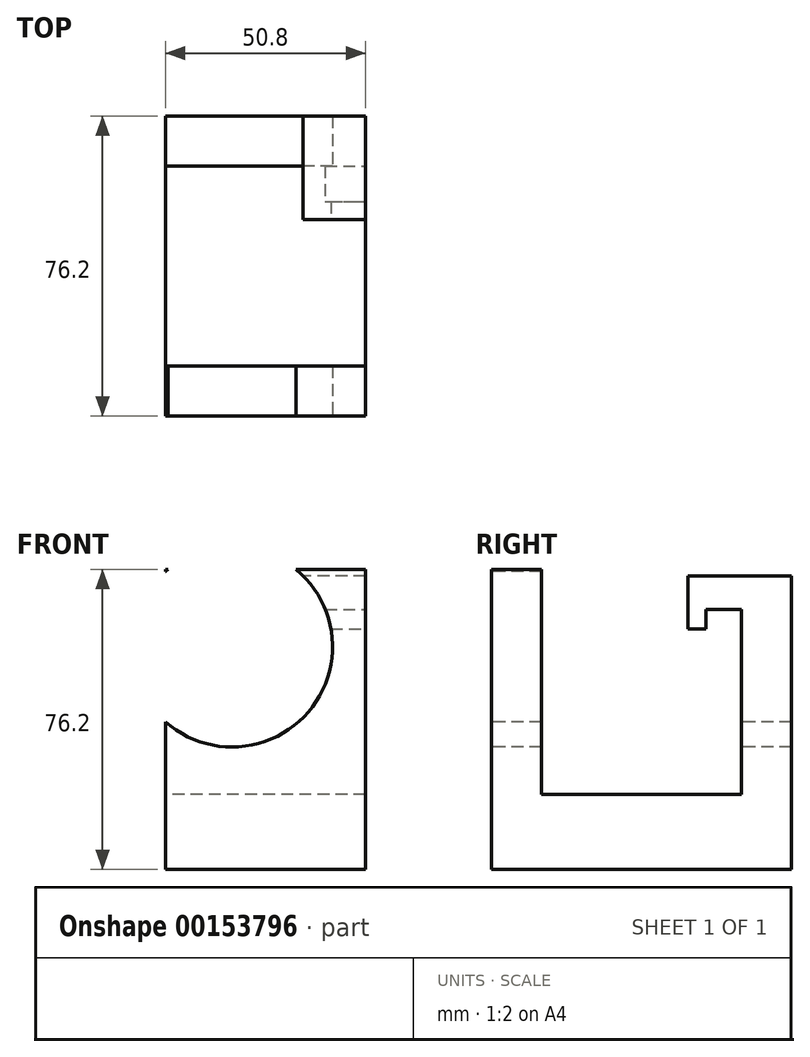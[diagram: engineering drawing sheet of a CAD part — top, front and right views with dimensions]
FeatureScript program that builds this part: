
annotation { "Feature Type Name" : "Feature", "Feature Type Description" : "" }
export const myFeature = defineFeature(function(context is Context, id is Id, definition is map)
    precondition{}
    {
        {
            var Q0;
            Q0=qCreatedBy(makeId("Right.planeOp"),FACE);
            var sketch = newSketch(context, id + "F0", { "sketchPlane" : qUnion([Q0])});
            skLineSegment(sketch, "E0", {"start": v(0, 0) * mm, "end": v(76.2, 0) * mm});
            skLineSegment(sketch, "E1", {"start": v(76.2, 0) * mm, "end": v(76.2, 74.55) * mm});
            skLineSegment(sketch, "E2", {"start": v(76.2, 74.55) * mm, "end": v(63.5, 74.55) * mm});
            skLineSegment(sketch, "E3", {"start": v(63.5, 74.55) * mm, "end": v(63.5, 19.05) * mm});
            skLineSegment(sketch, "E4", {"start": v(63.5, 19.05) * mm, "end": v(12.7, 19.05) * mm});
            skLineSegment(sketch, "E5", {"start": v(12.7, 19.05) * mm, "end": v(12.7, 76.2) * mm});
            skLineSegment(sketch, "E6", {"start": v(12.7, 76.2) * mm, "end": v(0, 76.2) * mm});
            skLineSegment(sketch, "E7", {"start": v(0, 76.2) * mm, "end": v(0, 0) * mm});
            skSolve(sketch);
        }
        {
            var Q0;
            Q0 = qSketchRegion(id + "F0", true);
            extrude(context, id + "F1", {"entities" : qUnion([Q0]), "depth" : 50.8 * mm});
        }
        {
            var Q0;
            Q0=makeQuery(id+"F1.opExtrude","CAP_FACE",FACE,{"disambiguationData":[OSD([sQuery(id+"F0.wireOp",EDGE,"E0"),sQuery(id+"F0.wireOp",EDGE,"E1"),sQuery(id+"F0.wireOp",EDGE,"E2"),sQuery(id+"F0.wireOp",EDGE,"E3"),sQuery(id+"F0.wireOp",EDGE,"E4"),sQuery(id+"F0.wireOp",EDGE,"E5"),sQuery(id+"F0.wireOp",EDGE,"E6"),sQuery(id+"F0.wireOp",EDGE,"E7")])],"isStart":false});
            var sketch = newSketch(context, id + "F2", { "sketchPlane" : qUnion([Q0])});
            skLineSegment(sketch, "E8", {"start": v(38.1, 0) * mm, "end": v(38.1, 88.9) * mm, "construction": true});
            skLineSegment(sketch, "E9", {"start": v(63.5, 74.55) * mm, "end": v(49.85, 74.55) * mm});
            skLineSegment(sketch, "E10", {"start": v(49.85, 74.55) * mm, "end": v(49.85, 61.04) * mm});
            skLineSegment(sketch, "E11", {"start": v(49.85, 61.04) * mm, "end": v(54.45, 61.04) * mm});
            skLineSegment(sketch, "E12", {"start": v(54.45, 61.04) * mm, "end": v(54.45, 66.1) * mm});
            skLineSegment(sketch, "E13", {"start": v(54.45, 66.1) * mm, "end": v(63.5, 66.1) * mm});
            skSolve(sketch);
        }
        {
            var Q0;
            Q0=makeQuery(id+"F1.opExtrude","SWEPT_FACE",FACE,{"disambiguationData":[OSD([sQuery(id+"F0.wireOp",EDGE,"E7")])]});
            var sketch = newSketch(context, id + "F3", { "sketchPlane" : qUnion([Q0])});
            skCircle(sketch, "E14", {"center": v(16.9, 56.58) * mm, "radius": 25.49 * mm});
            skSolve(sketch);
        }
        {
            var Q0;
            {var subQ0=sQuery(id+"F2.wireOp",EDGE,"E9");Q0=makeQuery(id+"F2.imprint","IMPRINT",FACE,{"disambiguationData":[TD([[makeQuery(id+"F2.imprint","IMPRINT",EDGE,{"derivedFrom":subQ0}),1.0]])]});}
            extrude(context, id + "F4", {"entities" : qUnion([Q0]), "operationType" : NewBodyOperationType.ADD, "oppositeDirection" : true, "depth" : 25.4 * mm});
        }
        {
            var Q0;
            Q0 = qSketchRegion(id + "F3", true);
            extrude(context, id + "F5", {"entities" : qUnion([Q0]), "operationType" : NewBodyOperationType.REMOVE, "endBound" : BoundingType.THROUGH_ALL, "oppositeDirection" : true, "depth" : 25.4 * mm});
        }
    });
